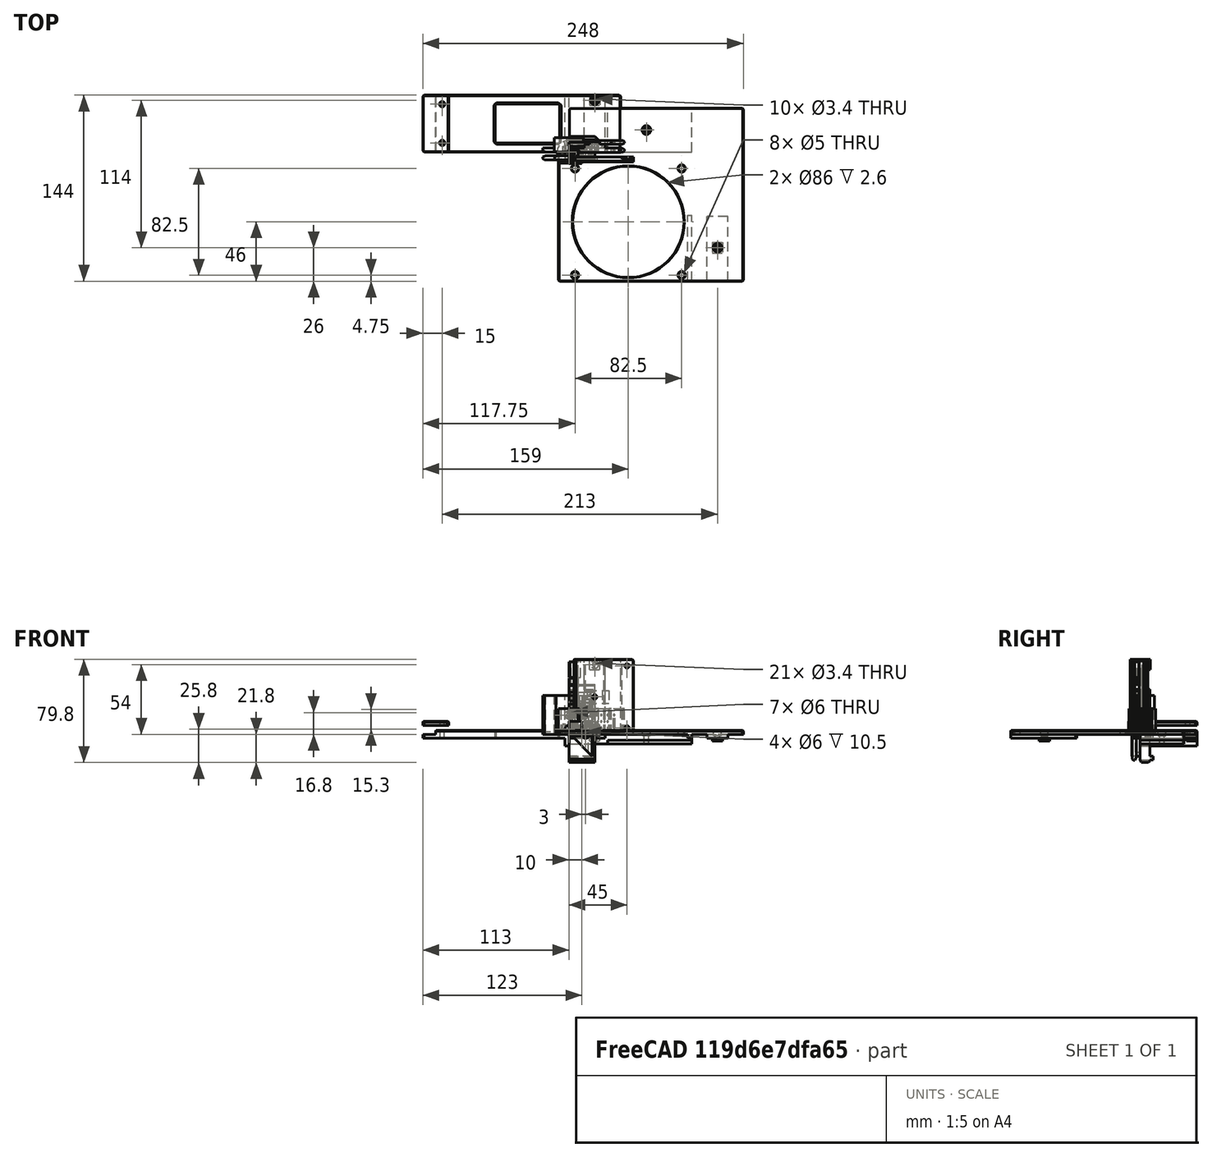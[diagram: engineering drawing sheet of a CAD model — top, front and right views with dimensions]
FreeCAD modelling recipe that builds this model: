
FCSTD DOCUMENT  (FreeCAD 0.18R16146 (Git))
Label: rack-clip-mounter
License: All rights reserved
LicenseURL: http://en.wikipedia.org/wiki/All_rights_reserved
objects: Part::Box×87, Part::Chamfer×70, Part::Cylinder×50, Part::MultiFuse×40, Part::Cut×40, Part::Feature×20, Part::MultiCommon×4, Part::Sphere×3, Part::FeaturePython×1
note: 315 computed .brp shape members not serialized (recipe doc carries the construction recipe); baked Part::Feature solids carry a one-line shape summary decoded from their .brp

FEATURE [Part::Box] Box  label="Cube"
  AttacherType = Attacher::AttachEngine3D
  Height = 8
  Length = 2.5
  Placement = pos=(-4.5,0,0) rot=(0,0,1;0rad)
  Width = 3.5
FEATURE [Part::Cylinder] Cylinder
  Angle = 360
  AttacherType = Attacher::AttachEngine3D
  Height = 8
  Placement = pos=(-4,2.5,0) rot=(0,0,1;0rad)
  Radius = 1
FEATURE [Part::Cylinder] Cylinder001
  Angle = 360
  AttacherType = Attacher::AttachEngine3D
  Height = 8
  Placement = pos=(4,2.5,0) rot=(0,0,1;0rad)
  Radius = 1
FEATURE [Part::Box] Box001  label="Cube001"
  AttacherType = Attacher::AttachEngine3D
  Height = 8
  Length = 2.5
  Placement = pos=(2,0,0) rot=(0,0,1;0rad)
  Width = 3.5
FEATURE [Part::Box] Box002  label="Cube002"
  AttacherType = Attacher::AttachEngine3D
  Height = 20
  Length = 16
  Placement = pos=(-8,-2.5,0) rot=(0,0,1;0rad)
  Width = 2.5
FEATURE [Part::Box] Box003  label="Cube003"
  AttacherType = Attacher::AttachEngine3D
  Height = 3
  Length = 10
  Width = 7
FEATURE [Part::Box] Box004  label="Cube004"
  AttacherType = Attacher::AttachEngine3D
  Height = 10
  Length = 10
  Placement = pos=(0,4,0) rot=(0,0,1;0rad)
  Width = 3
FEATURE [Part::Box] Box005  label="Cube005"
  AttacherType = Attacher::AttachEngine3D
  Height = 10
  Length = 10
  Placement = pos=(0,-9,0) rot=(0,0,1;0rad)
  Width = 9
FEATURE [Part::MultiFuse] Fusion001
  Shapes = -> [Box005,Box003,Box004]
FEATURE [Part::Box] Box006  label="Cube006"
  AttacherType = Attacher::AttachEngine3D
  Height = 20
  Length = 16
  Placement = pos=(-8,-8,0) rot=(0,0,1;0rad)
  Width = 2.5
FEATURE [Part::Box] Box007  label="Cube007"
  AttacherType = Attacher::AttachEngine3D
  Height = 20
  Length = 3
  Placement = pos=(5,-8,0) rot=(0,0,1;0rad)
  Width = 8
FEATURE [Part::MultiFuse] Fusion
  Shapes = -> [Cylinder,Box006,Box,Box007,Cylinder001,Box001,Box002]
FEATURE [Part::Chamfer] Chamfer
  Base = -> Fusion
  Edges = 1 edges: [Edge50 r1=2 r2=1]
FEATURE [Part::Chamfer] Chamfer001
  Base = -> Chamfer
  Edges = 1 edges: [Edge71 r1=2 r2=1]
FEATURE [Part::Chamfer] Chamfer002
  Base = -> Chamfer001
  Edges = 1 edges r=1: [Edge32]
FEATURE [Part::Box] Box008  label="Cube008"
  AttacherType = Attacher::AttachEngine3D
  Height = 8
  Length = 2.5
  Placement = pos=(-4.5,2.5,0) rot=(0,0,1;0rad)
  Width = 2
FEATURE [Part::Box] Box009  label="Cube009"
  AttacherType = Attacher::AttachEngine3D
  Height = 8
  Length = 2.5
  Placement = pos=(2,2.5,0) rot=(0,0,1;0rad)
  Width = 2
FEATURE [Part::MultiFuse] Fusion002
  Shapes = -> [Chamfer002,Box008,Box009]
FEATURE [Part::Cylinder] Cylinder002
  Angle = 360
  AttacherType = Attacher::AttachEngine3D
  Height = 10
  Placement = pos=(0,-5,4) rot=(1,0,0;1.5708rad)
  Radius = 3
FEATURE [Part::Cut] Cut  label="side-clip"
  Base = -> Fusion002
  Tool = -> Cylinder002
FEATURE [Part::Box] Box010  label="Cube010"
  AttacherType = Attacher::AttachEngine3D
  Height = 30
  Length = 22.6
  Placement = pos=(-11.3,0,0) rot=(0,0,1;0rad)
  Width = 11
FEATURE [Part::Box] Box011  label="Cube011"
  AttacherType = Attacher::AttachEngine3D
  Height = 30
  Length = 6
  Placement = pos=(-3,-6,0) rot=(0,0,1;0rad)
  Width = 6
FEATURE [Part::Box] Box012  label="Cube012"
  AttacherType = Attacher::AttachEngine3D
  Height = 30
  Length = 40
  Placement = pos=(-20,0,0) rot=(0,0,1;0rad)
  Width = 3
FEATURE [Part::Box] Box013  label="Cube013"
  AttacherType = Attacher::AttachEngine3D
  Height = 30
  Length = 40
  Placement = pos=(-20,-6,0) rot=(0,0,1;0rad)
  Width = 3
FEATURE [Part::Cylinder] Cylinder003
  Angle = 360
  AttacherType = Attacher::AttachEngine3D
  Height = 30
  Placement = pos=(0,5,15) rot=(1,0,0;1.5708rad)
  Radius = 3
FEATURE [Part::Cylinder] Cylinder004
  Angle = 360
  AttacherType = Attacher::AttachEngine3D
  Height = 30
  Placement = pos=(0,18,15) rot=(1,0,0;1.5708rad)
  Radius = 1.7
FEATURE [Part::Box] Box014  label="Cube014"
  AttacherType = Attacher::AttachEngine3D
  Height = 30
  Length = 22.6
  Placement = pos=(-11.3,0,0) rot=(0,0,1;0rad)
  Width = 11
FEATURE [Part::Box] Box015  label="Cube015"
  AttacherType = Attacher::AttachEngine3D
  Height = 30
  Length = 3.3
  Placement = pos=(8,-6,0) rot=(0,0,1;0rad)
  Width = 6
FEATURE [Part::Box] Box016  label="Cube016"
  AttacherType = Attacher::AttachEngine3D
  Height = 30
  Length = 20
  Placement = pos=(-11,-6,0) rot=(0,0,1;0rad)
  Width = 3
FEATURE [Part::Cylinder] Cylinder005
  Angle = 360
  AttacherType = Attacher::AttachEngine3D
  Height = 25
  Placement = pos=(0,5,15) rot=(1,0,0;1.5708rad)
  Radius = 3
FEATURE [Part::MultiFuse] Fusion004
  Shapes = -> [Box016,Box014,Box015]
FEATURE [Part::Chamfer] Chamfer008
  Base = -> Fusion004
  Edges = 1 edges r=1: [Edge24]
FEATURE [Part::Chamfer] Chamfer009
  Base = -> Chamfer008
  Edges = 1 edges: [Edge38 r1=1 r2=2]
FEATURE [Part::Chamfer] Chamfer010
  Base = -> Chamfer009
  Edges = 1 edges: [Edge39 r1=2 r2=1]
FEATURE [Part::Cylinder] Cylinder006
  Angle = 360
  AttacherType = Attacher::AttachEngine3D
  Height = 25
  Placement = pos=(0,16,15) rot=(1,0,0;1.5708rad)
  Radius = 1.7
FEATURE [Part::Cut] Cut003
  Base = -> Chamfer010
  Tool = -> Cylinder006
FEATURE [Part::Cut] Cut004
  Base = -> Cut003
  Tool = -> Cylinder005
FEATURE [Part::Chamfer] Chamfer011  label="clip-back-top-bottom"
  Base = -> Cut004
  Edges = 1 edges r=1: [Edge23]
FEATURE [Part::Cylinder] Cylinder007
  Angle = 360
  AttacherType = Attacher::AttachEngine3D
  Height = 2
  Radius = 1.7
FEATURE [Part::Cylinder] Cylinder008
  Angle = 360
  AttacherType = Attacher::AttachEngine3D
  Height = 2
  Radius = 9
FEATURE [Part::Cut] Cut005  label="washer"
  Base = -> Cylinder008
  Tool = -> Cylinder007
FEATURE [Part::MultiFuse] Fusion005
  Shapes = -> [Box010,Box012,Box011,Box013]
FEATURE [Part::Chamfer] Chamfer012
  Base = -> Fusion005
  Edges = 3 edges: [Edge29 r1=2 r2=1,Edge55 r1=2 r2=1,Edge59 r1=2 r2=1]
FEATURE [Part::Chamfer] Chamfer013
  Base = -> Chamfer012
  Edges = 1 edges: [Edge48 r1=1 r2=2]
FEATURE [Part::Chamfer] Chamfer014
  Base = -> Chamfer013
  Edges = 2 edges r=1: [Edge85,Edge86]
FEATURE [Part::Cut] Cut006
  Base = -> Chamfer014
  Tool = -> Cylinder003
FEATURE [Part::Cut] Cut007  label="ckip-back-mid"
  Base = -> Cut006
  Tool = -> Cylinder004
FEATURE [Part::Box] Box017  label="Cube017"
  AttacherType = Attacher::AttachEngine3D
  Height = 41.6
  Length = 20
  Placement = pos=(0,0,-3) rot=(0,0,1;0rad)
  Width = 4.5
FEATURE [Part::Box] Box018  label="Cube018"
  AttacherType = Attacher::AttachEngine3D
  Height = 8.5
  Length = 20
  Placement = pos=(0,-6,-3) rot=(0,0,1;0rad)
  Width = 6
FEATURE [Part::Box] Box019  label="Cube019"
  AttacherType = Attacher::AttachEngine3D
  Height = 30
  Length = 20
  Placement = pos=(0,-6,-3) rot=(0,0,1;0rad)
  Width = 3
FEATURE [Part::Cylinder] Cylinder009
  Angle = 360
  AttacherType = Attacher::AttachEngine3D
  Height = 17
  Placement = pos=(10,3,19.3) rot=(1,0,0;1.5708rad)
  Radius = 3
FEATURE [Part::Cylinder] Cylinder010
  Angle = 360
  AttacherType = Attacher::AttachEngine3D
  Height = 17
  Placement = pos=(10,6,19.3) rot=(1,0,0;1.5708rad)
  Radius = 1.7
FEATURE [Part::Cylinder] Cylinder011
  Angle = 360
  AttacherType = Attacher::AttachEngine3D
  Height = 2
  Placement = pos=(10,5.5,19.3) rot=(1,0,0;1.5708rad)
  Radius = 2.9
FEATURE [Part::Box] Box020  label="Cube020"
  AttacherType = Attacher::AttachEngine3D
  Height = 3
  Length = 20
  Placement = pos=(0,-6,-3) rot=(0,0,1;0rad)
  Width = 13
FEATURE [Part::Box] Box021  label="Cube021"
  AttacherType = Attacher::AttachEngine3D
  Height = 41.6
  Length = 20
  Placement = pos=(0,0,-3) rot=(0,0,1;0rad)
  Width = 4.5
FEATURE [Part::Box] Box022  label="Cube022"
  AttacherType = Attacher::AttachEngine3D
  Height = 3
  Length = 20
  Placement = pos=(0,0,-3) rot=(0,0,1;0rad)
  Width = 7
FEATURE [Part::Box] Box023  label="Cube023"
  AttacherType = Attacher::AttachEngine3D
  Height = 8.5
  Length = 20
  Placement = pos=(0,-6,30.1) rot=(0,0,1;0rad)
  Width = 6
FEATURE [Part::Box] Box024  label="Cube024"
  AttacherType = Attacher::AttachEngine3D
  Height = 30
  Length = 20
  Placement = pos=(0,-6,8.6) rot=(0,0,1;0rad)
  Width = 3
FEATURE [Part::MultiFuse] Fusion007
  Shapes = -> [Box024,Box023,Box022,Box021]
FEATURE [Part::Cylinder] Cylinder012
  Angle = 360
  AttacherType = Attacher::AttachEngine3D
  Height = 15
  Placement = pos=(10,7,19.3) rot=(1,0,0;1.5708rad)
  Radius = 1.7
FEATURE [Part::Chamfer] Chamfer015
  Base = -> Cylinder011
  Edges = 1 edges r=1: [Edge3]
FEATURE [Part::MultiFuse] Fusion008
  Shapes = -> [Box019,Box018,Box017,Box020]
FEATURE [Part::Chamfer] Chamfer016
  Base = -> Fusion008
  Edges = 1 edges: [Edge36 r1=1 r2=2]
FEATURE [Part::Chamfer] Chamfer017
  Base = -> Chamfer016
  Edges = 1 edges r=1: [Edge34]
FEATURE [Part::MultiFuse] Fusion009
  Shapes = -> [Chamfer017,Chamfer015]
FEATURE [Part::Cut] Cut008
  Base = -> Fusion009
  Tool = -> Cylinder010
FEATURE [Part::Chamfer] Chamfer018
  Base = -> Cut008
  Edges = 1 edges r=1: [Edge77]
FEATURE [Part::Cut] Cut009  label="clip-side-bottom-corner"
  Base = -> Chamfer018
  Tool = -> Cylinder009
FEATURE [Part::Cylinder] Cylinder013
  Angle = 360
  AttacherType = Attacher::AttachEngine3D
  Height = 2
  Placement = pos=(10,5.5,19.3) rot=(1,0,0;1.5708rad)
  Radius = 2.9
FEATURE [Part::Cylinder] Cylinder014
  Angle = 360
  AttacherType = Attacher::AttachEngine3D
  Height = 15
  Placement = pos=(10,3,19.3) rot=(1,0,0;1.5708rad)
  Radius = 3
FEATURE [Part::Chamfer] Chamfer019
  Base = -> Cylinder013
  Edges = 1 edges r=1: [Edge3]
FEATURE [Part::Chamfer] Chamfer020
  Base = -> Fusion007
  Edges = 1 edges: [Edge13 r1=2 r2=1]
FEATURE [Part::Chamfer] Chamfer021
  Base = -> Chamfer020
  Edges = 3 edges r=1: [Edge14,Edge23,Edge38]
FEATURE [Part::MultiFuse] Fusion010
  Shapes = -> [Chamfer021,Chamfer019]
FEATURE [Part::Cut] Cut010
  Base = -> Fusion010
  Tool = -> Cylinder012
FEATURE [Part::Cut] Cut011  label="clip-side-top-corner"
  Base = -> Cut010
  Tool = -> Cylinder014
FEATURE [Part::Box] Box025  label="Cube025"
  AttacherType = Attacher::AttachEngine3D
  Height = 36.6
  Length = 20
  Placement = pos=(0,0,-3) rot=(0,0,1;0rad)
  Width = 7.5
FEATURE [Part::Box] Box026  label="Cube026"
  AttacherType = Attacher::AttachEngine3D
  Height = 6
  Length = 20
  Placement = pos=(0,-6,-3) rot=(0,0,1;0rad)
  Width = 6
FEATURE [Part::Box] Box027  label="Cube027"
  AttacherType = Attacher::AttachEngine3D
  Height = 3
  Length = 20
  Placement = pos=(0,-6,-3) rot=(0,0,1;0rad)
  Width = 16
FEATURE [Part::Box] Box028  label="Cube028"
  AttacherType = Attacher::AttachEngine3D
  Height = 27.5
  Length = 20
  Placement = pos=(0,-6,-3) rot=(0,0,1;0rad)
  Width = 3
FEATURE [Part::Cylinder] Cylinder015
  Angle = 360
  AttacherType = Attacher::AttachEngine3D
  Height = 20
  Placement = pos=(10,5,16.8) rot=(1,0,0;1.5708rad)
  Radius = 3
FEATURE [Part::Cylinder] Cylinder016
  Angle = 360
  AttacherType = Attacher::AttachEngine3D
  Height = 20
  Placement = pos=(10,12,16.8) rot=(1,0,0;1.5708rad)
  Radius = 1.7
FEATURE [Part::Cylinder] Cylinder017
  Angle = 360
  AttacherType = Attacher::AttachEngine3D
  Height = 20
  Placement = pos=(10,12,16.8) rot=(1,0,0;1.5708rad)
  Radius = 1.7
FEATURE [Part::Cylinder] Cylinder018
  Angle = 360
  AttacherType = Attacher::AttachEngine3D
  Height = 20
  Placement = pos=(10,5,16.8) rot=(1,0,0;1.5708rad)
  Radius = 3
FEATURE [Part::Box] Box029  label="Cube029"
  AttacherType = Attacher::AttachEngine3D
  Height = 27.5
  Length = 20
  Placement = pos=(0,-6,6.1) rot=(0,0,1;0rad)
  Width = 3
FEATURE [Part::Box] Box030  label="Cube030"
  AttacherType = Attacher::AttachEngine3D
  Height = 3
  Length = 20
  Placement = pos=(0,0,-3) rot=(0,0,1;0rad)
  Width = 10
FEATURE [Part::Box] Box031  label="Cube031"
  AttacherType = Attacher::AttachEngine3D
  Height = 6
  Length = 20
  Placement = pos=(0,-6,27.6) rot=(0,0,1;0rad)
  Width = 6
FEATURE [Part::Box] Box032  label="Cube032"
  AttacherType = Attacher::AttachEngine3D
  Height = 36.6
  Length = 20
  Placement = pos=(0,0,-3) rot=(0,0,1;0rad)
  Width = 7.5
FEATURE [Part::MultiFuse] Fusion011
  Shapes = -> [Box028,Box026,Box025,Box027]
FEATURE [Part::Chamfer] Chamfer022
  Base = -> Fusion011
  Edges = 1 edges: [Edge36 r1=1 r2=2]
FEATURE [Part::Chamfer] Chamfer023
  Base = -> Chamfer022
  Edges = 3 edges r=1: [Edge7,Edge31,Edge34]
FEATURE [Part::Cut] Cut012
  Base = -> Chamfer023
  Tool = -> Cylinder015
FEATURE [Part::Cut] Cut013  label="clip-side-bottom-center"
  Base = -> Cut012
  Tool = -> Cylinder016
FEATURE [Part::MultiFuse] Fusion012
  Shapes = -> [Box029,Box031,Box032,Box030]
FEATURE [Part::Chamfer] Chamfer024
  Base = -> Fusion012
  Edges = 1 edges: [Edge13 r1=2 r2=1]
FEATURE [Part::Chamfer] Chamfer025
  Base = -> Chamfer024
  Edges = 3 edges r=1: [Edge14,Edge23,Edge38]
FEATURE [Part::Cut] Cut014
  Base = -> Chamfer025
  Tool = -> Cylinder018
FEATURE [Part::Cut] Cut015  label="clip-side-top-center"
  Base = -> Cut014
  Tool = -> Cylinder017
FEATURE [Part::Box] Box033  label="Cube033"
  AttacherType = Attacher::AttachEngine3D
  Height = 43.6
  Length = 20
  Placement = pos=(0,0,-21.8) rot=(0,0,1;0rad)
  Width = 7.5
FEATURE [Part::Box] Box034  label="Cube034"
  AttacherType = Attacher::AttachEngine3D
  Height = 3
  Length = 20
  Placement = pos=(0,0,-19.8) rot=(0,0,1;0rad)
  Width = 10
FEATURE [Part::Box] Box035  label="Cube035"
  AttacherType = Attacher::AttachEngine3D
  Height = 6
  Length = 20
  Placement = pos=(0,-6,-3) rot=(0,0,1;0rad)
  Width = 6
FEATURE [Part::Box] Box036  label="Cube036"
  AttacherType = Attacher::AttachEngine3D
  Height = 40
  Length = 20
  Placement = pos=(0,-6,-20) rot=(0,0,1;0rad)
  Width = 3
FEATURE [Part::MultiFuse] Fusion013
  Shapes = -> [Box036,Box035,Box034,Box033]
FEATURE [Part::Chamfer] Chamfer026
  Base = -> Fusion013
  Edges = 1 edges: [Edge30 r1=1 r2=2]
FEATURE [Part::Chamfer] Chamfer027
  Base = -> Chamfer026
  Edges = 1 edges: [Edge45 r1=2 r2=1]
FEATURE [Part::Chamfer] Chamfer028
  Base = -> Chamfer027
  Edges = 1 edges: [Edge57 r1=2 r2=1]
FEATURE [Part::Chamfer] Chamfer029
  Base = -> Chamfer028
  Edges = 1 edges: [Edge64 r1=1.9 r2=1]
FEATURE [Part::Chamfer] Chamfer030
  Base = -> Chamfer029
  Edges = 4 edges r=1: [Edge14,Edge44,Edge85,Edge86]
FEATURE [Part::Cylinder] Cylinder019
  Angle = 360
  AttacherType = Attacher::AttachEngine3D
  Height = 19
  Placement = pos=(10,4.5,-1e-15) rot=(1,0,0;1.5708rad)
  Radius = 3
FEATURE [Part::Cylinder] Cylinder020
  Angle = 360
  AttacherType = Attacher::AttachEngine3D
  Height = 19
  Placement = pos=(10,9,-2e-15) rot=(1,0,0;1.5708rad)
  Radius = 1.7
FEATURE [Part::Cut] Cut016
  Base = -> Chamfer030
  Tool = -> Cylinder020
FEATURE [Part::Cut] Cut017  label="clip-side-mid-center"
  Base = -> Cut016
  Tool = -> Cylinder019
FEATURE [Part::Box] Box037  label="Cube037"
  AttacherType = Attacher::AttachEngine3D
  Height = 36.6
  Length = 18
  Placement = pos=(0,0,-19.8) rot=(0,0,1;0rad)
  Width = 7.5
FEATURE [Part::Box] Box038  label="Cube038"
  AttacherType = Attacher::AttachEngine3D
  Height = 3
  Length = 18
  Placement = pos=(0,0,-19.8) rot=(0,0,1;0rad)
  Width = 10
FEATURE [Part::Box] Box039  label="Cube039"
  AttacherType = Attacher::AttachEngine3D
  Height = 3.6
  Length = 18
  Placement = pos=(0,-6.5,-1.8) rot=(0,0,1;0rad)
  Width = 8
FEATURE [Part::Feature] Body001
  shape: bbox 18 x 6.5 x 18 mm, 5 faces (baked)
FEATURE [Part::Feature] Body002
  Placement = pos=(-3,3,3) rot=(0,0,1;0rad)
  shape: bbox 18 x 6.5 x 18 mm, 5 faces (baked)
FEATURE [Part::Cut] Cut018  label="corner-mount-slot"
  Base = -> Body001
  Placement = pos=(0,0,-1.2) rot=(0,0,1;0rad)
  Tool = -> Body002
FEATURE [Part::Feature] Cut018001  label="Cut019"
  Placement = pos=(0,0,-1.2) rot=(0,0,1;0rad)
  shape: bbox 18 x 6.5 x 18 mm, 8 faces (baked)
FEATURE [Part::Feature] Part__Mirroring001  label="Cut019 (Mirror #1)001"
  Placement = pos=(0,0,1e-16) rot=(0,0,1;0rad)
  shape: bbox 18 x 6.5 x 18 mm, 8 faces (baked)
FEATURE [Part::Cylinder] Cylinder021
  Angle = 360
  AttacherType = Attacher::AttachEngine3D
  Height = 23
  Placement = pos=(13,12,-3e-15) rot=(1,0,0;1.5708rad)
  Radius = 1.7
FEATURE [Part::MultiFuse] Fusion014
  Shapes = -> [Cut018001,Part__Mirroring001,Box039,Box038,Box037]
FEATURE [Part::Cylinder] Cylinder022
  Angle = 360
  AttacherType = Attacher::AttachEngine3D
  Height = 23
  Placement = pos=(13,4,-1.2e-15) rot=(1,0,0;1.5708rad)
  Radius = 3
FEATURE [Part::Cut] Cut018002
  Base = -> Fusion014
  Tool = -> Cylinder021
FEATURE [Part::Cut] Cut018003  label="acrilic-mid-cirner"
  Base = -> Cut018002
  Tool = -> Cylinder022
FEATURE [Part::Feature] Cut018004  label="side-clip001"
  shape: bbox 16 x 12.5 x 20 mm, 71 faces (baked)
FEATURE [Part::Box] Box040  label="Cube040"
  AttacherType = Attacher::AttachEngine3D
  Height = 24
  Length = 22
  Placement = pos=(-12,-5,0) rot=(0,0,1;0rad)
  Width = 14
FEATURE [Part::Feature] Cut018005  label="side-clip002"
  shape: bbox 16 x 12.5 x 20 mm, 71 faces (baked)
FEATURE [Part::Box] Box041  label="Cube041"
  AttacherType = Attacher::AttachEngine3D
  Height = 24
  Length = 22
  Placement = pos=(-12,-17,0) rot=(0,0,1;0rad)
  Width = 14
FEATURE [Part::MultiCommon] Common
  Placement = pos=(0,-0.5,0) rot=(0,0,1;0rad)
  Shapes = -> [Box041,Cut018004]
FEATURE [Part::MultiCommon] Common001
  Shapes = -> [Cut018005,Box040]
FEATURE [Part::MultiFuse] Fusion015  label="side-clip-wide"
  Shapes = -> [Common,Common001]
FEATURE [Part::Feature] Cut018006  label="corner-mount-slot001"
  Placement = pos=(2,0,17) rot=(0,0,1;0rad)
  shape: bbox 18 x 6.5 x 18 mm, 8 faces (baked)
FEATURE [Part::Box] Box042  label="Cube042"
  AttacherType = Attacher::AttachEngine3D
  Height = 38
  Length = 20
  Placement = pos=(0,0,-3) rot=(0,0,1;0rad)
  Width = 7.5
FEATURE [Part::Box] Box043  label="Cube043"
  AttacherType = Attacher::AttachEngine3D
  Height = 3
  Length = 20
  Placement = pos=(0,0,-3) rot=(0,0,1;0rad)
  Width = 10
FEATURE [Part::Cylinder] Cylinder023
  Angle = 360
  AttacherType = Attacher::AttachEngine3D
  Height = 21
  Placement = pos=(10,4,16.8) rot=(1,0,0;1.5708rad)
  Radius = 3
FEATURE [Part::MultiFuse] Fusion016
  Shapes = -> [Box043,Cut018006,Box042]
FEATURE [Part::Cylinder] Cylinder024
  Angle = 360
  AttacherType = Attacher::AttachEngine3D
  Height = 21
  Placement = pos=(10,12,16.8) rot=(1,0,0;1.5708rad)
  Radius = 1.7
FEATURE [Part::Cut] Cut018007
  Base = -> Fusion016
  Tool = -> Cylinder024
FEATURE [Part::Cut] Cut018008
  Base = -> Cut018007
  Tool = -> Cylinder023
FEATURE [Part::Chamfer] Chamfer031  label="acrilic-corner-btm"
  Base = -> Cut018008
  Edges = 1 edges r=1: [Edge5]
FEATURE [Part::Box] Box044  label="Cube044"
  AttacherType = Attacher::AttachEngine3D
  Height = 36.6
  Length = 20
  Placement = pos=(0,0,-3) rot=(0,0,1;0rad)
  Width = 7.5
FEATURE [Part::Feature] Part__Mirroring002  label="corner-mount-slot002 (Mirror #1)001"
  Placement = pos=(2,0,15.4) rot=(0,0,1;0rad)
  shape: bbox 18 x 6.5 x 18 mm, 8 faces (baked)
FEATURE [Part::Box] Box045  label="Cube045"
  AttacherType = Attacher::AttachEngine3D
  Height = 3
  Length = 20
  Placement = pos=(0,0,-3) rot=(0,0,1;0rad)
  Width = 10
FEATURE [Part::MultiFuse] Fusion017
  Shapes = -> [Box045,Part__Mirroring002,Box044]
FEATURE [Part::Chamfer] Chamfer032
  Base = -> Fusion017
  Edges = 2 edges r=1: [Edge5,Edge32]
FEATURE [Part::Cylinder] Cylinder025
  Angle = 360
  AttacherType = Attacher::AttachEngine3D
  Height = 21
  Placement = pos=(10,12,16.8) rot=(1,0,0;1.5708rad)
  Radius = 1.7
FEATURE [Part::Cylinder] Cylinder026
  Angle = 360
  AttacherType = Attacher::AttachEngine3D
  Height = 21
  Placement = pos=(10,4,16.8) rot=(1,0,0;1.5708rad)
  Radius = 3
FEATURE [Part::Cut] Cut018009
  Base = -> Chamfer032
  Tool = -> Cylinder025
FEATURE [Part::Cut] Cut018010  label="acrilic-corner-top"
  Base = -> Cut018009
  Tool = -> Cylinder026
FEATURE [Part::Box] Box051008  label="Cube065"
  AttacherType = Attacher::AttachEngine3D
  Height = 3
  Length = 9
  Placement = pos=(-8,-100,0) rot=(0,0,1;0rad)
  Width = 99
FEATURE [Part::Chamfer] Chamfer034004
  Base = -> Box051008
  Edges = 2 edges r=1: [Edge1,Edge3]
FEATURE [Part::Chamfer] Chamfer034005
  Base = -> Chamfer034004
  Edges = 5 edges r=0.4: [Edge1,Edge5,Edge6,Edge7,Edge8]
FEATURE [Part::Feature] Chamfer034005001  label="Chamfer034006"
  shape: bbox 9 x 99 x 3 mm, 13 faces (baked)
FEATURE [Part::Box] Box051009  label="Cube066"
  AttacherType = Attacher::AttachEngine3D
  Height = 3
  Length = 40
  Width = 44
FEATURE [Part::Box] Box051010  label="Cube067"
  AttacherType = Attacher::AttachEngine3D
  Height = 3
  Length = 16
  Placement = pos=(12,0,-3) rot=(0,0,1;0rad)
  Width = 44
FEATURE [Part::Box] Box051011  label="Cube068"
  AttacherType = Attacher::AttachEngine3D
  Height = 3
  Length = 8
  Placement = pos=(16,36,-5) rot=(0,0,1;0rad)
  Width = 8
FEATURE [Part::Feature] Chamfer034005002001  label="Chamfer034005003"
  shape: bbox 135 x 134 x 10.5 mm, 37 faces (baked)
FEATURE [Part::Chamfer] Chamfer034005002002
  Base = -> Chamfer034005002001
  Edges = 15 edges r=0.4: [Edge1,Edge18,Edge42,Edge43,Edge46,Edge70,Edge78,Edge79,Edge81,Edge83,Edge85,Edge87,Edge89,Edge93,Edge95]
FEATURE [Part::MultiFuse] Fusion021005002  label="fan-mount-btm"
  Shapes = -> [Chamfer034005,Chamfer034005002002]
FEATURE [Part::Feature] Cut018011002001  label="Cut018011003"
  shape: bbox 135 x 134 x 10.5 mm, 35 faces (baked)
FEATURE [Part::Chamfer] Chamfer034005002003
  Base = -> Cut018011002001
  Edges = 4 edges r=1: [Edge41,Edge43,Edge80,Edge82]
FEATURE [Part::Chamfer] Chamfer034005002004
  Base = -> Chamfer034005002003
  Edges = 15 edges r=0.4: [Edge25,Edge33,Edge36,Edge50,Edge58,Edge61,Edge64,Edge65,Edge67,Edge69,Edge71,Edge73,Edge75,Edge76,Edge77]
FEATURE [Part::MultiFuse] Fusion021005003  label="fan-mount-top"
  Shapes = -> [Chamfer034005001,Chamfer034005002004]
FEATURE [Part::MultiFuse] Fusion021005004
  Shapes = -> [Box051011,Box051010,Box051009]
FEATURE [Part::Box] Box051012  label="Cube069"
  AttacherType = Attacher::AttachEngine3D
  Height = 6
  Length = 103
  Placement = pos=(-103,0,-3) rot=(0,0,1;0rad)
  Width = 44
FEATURE [Part::Box] Box051013  label="Cube070"
  AttacherType = Attacher::AttachEngine3D
  Height = 3
  Length = 10
  Placement = pos=(-113,0,-3) rot=(0,0,1;0rad)
  Width = 44
FEATURE [Part::Box] Box051014  label="Cube071"
  AttacherType = Attacher::AttachEngine3D
  Height = 6
  Length = 50
  Placement = pos=(-57,7,-3) rot=(0,0,1;0rad)
  Width = 30
FEATURE [Part::Box] Box051015  label="Cube072"
  AttacherType = Attacher::AttachEngine3D
  Height = 6
  Length = 3
  Placement = pos=(-3,0,-9) rot=(0,0,1;0rad)
  Width = 44
FEATURE [Part::Cylinder] Cylinder027
  Angle = 360
  AttacherType = Attacher::AttachEngine3D
  Height = 10
  Placement = pos=(20,40,-5) rot=(0,0,1;0rad)
  Radius = 1.7
FEATURE [Part::Cylinder] Cylinder028
  Angle = 360
  AttacherType = Attacher::AttachEngine3D
  Height = 10
  Placement = pos=(20,40,-1) rot=(0,0,1;0rad)
  Radius = 3
FEATURE [Part::MultiFuse] Fusion021005005
  Shapes = -> [Cylinder028,Cylinder027]
FEATURE [Part::MultiFuse] Fusion021005006
  Shapes = -> [Box051012,Box051013,Box051015,Fusion021005004]
FEATURE [Part::Cut] Cut018011002002
  Base = -> Fusion021005006
  Tool = -> Fusion021005005
FEATURE [Part::Cut] Cut018011002003
  Base = -> Cut018011002002
  Tool = -> Box051014
FEATURE [Part::Box] Box051016  label="Cube073"
  AttacherType = Attacher::AttachEngine3D
  Height = 3
  Length = 20
  Placement = pos=(-113,0,7) rot=(0,0,1;0rad)
  Width = 44
FEATURE [Part::Cylinder] Cylinder029
  Angle = 360
  AttacherType = Attacher::AttachEngine3D
  Height = 30
  Placement = pos=(-98,7,-7) rot=(0,0,1;0rad)
  Radius = 1.7
FEATURE [Part::Cylinder] Cylinder030
  Angle = 360
  AttacherType = Attacher::AttachEngine3D
  Height = 30
  Placement = pos=(-98,37,-7) rot=(0,0,1;0rad)
  Radius = 1.7
FEATURE [Part::Cylinder] Cylinder031
  Angle = 360
  AttacherType = Attacher::AttachEngine3D
  Height = 30
  Placement = pos=(-98,37,-7) rot=(0,0,1;0rad)
  Radius = 1.7
FEATURE [Part::Cylinder] Cylinder032
  Angle = 360
  AttacherType = Attacher::AttachEngine3D
  Height = 30
  Placement = pos=(-98,7,-7) rot=(0,0,1;0rad)
  Radius = 1.7
FEATURE [Part::MultiFuse] Fusion021005007
  Shapes = -> [Cylinder032,Cylinder031]
FEATURE [Part::Cut] Cut018011002004
  Base = -> Cut018011002003
  Tool = -> Fusion021005007
FEATURE [Part::MultiFuse] Fusion021005008
  Shapes = -> [Cylinder029,Cylinder030]
FEATURE [Part::Cut] Cut018011002005
  Base = -> Box051016
  Tool = -> Fusion021005008
FEATURE [Part::Chamfer] Chamfer034005002005
  Base = -> Cut018011002004
  Edges = 12 edges r=1: [Edge15,Edge16,Edge17,Edge18,Edge43,Edge46,Edge52,Edge53,Edge54,Edge55,Edge62,Edge64]
FEATURE [Part::Chamfer] Chamfer034005002006  label="cable-route-base"
  Base = -> Chamfer034005002005
  Edges = 11 edges r=0.4: [Edge9,Edge10,Edge11,Edge13,Edge14,Edge44,Edge45,Edge46,Edge47,Edge48,Edge49]
FEATURE [Part::Chamfer] Chamfer034005002007
  Base = -> Cut018011002005
  Edges = 4 edges r=1: [Edge1,Edge3,Edge6,Edge13]
FEATURE [Part::Chamfer] Chamfer034005002008  label="cable-route-cap"
  Base = -> Chamfer034005002007
  Edges = 10 edges r=0.4: [Edge1,Edge5,Edge6,Edge7,Edge8,Edge9,Edge10,Edge11,Edge12,Edge13]
FEATURE [Part::Box] Box051017  label="Cube074"
  AttacherType = Attacher::AttachEngine3D
  Height = 20
  Length = 33
  Width = 3
FEATURE [Part::Box] Box051018  label="Cube075"
  AttacherType = Attacher::AttachEngine3D
  Height = 20
  Length = 10
  Placement = pos=(0,6.5,0) rot=(0,0,1;0rad)
  Width = 3
FEATURE [Part::Box] Box051019  label="Cube076"
  AttacherType = Attacher::AttachEngine3D
  Height = 20
  Length = 20
  Placement = pos=(13,6,0) rot=(0,0,1;0rad)
  Width = 3
FEATURE [Part::Box] Box051020  label="Cube077"
  AttacherType = Attacher::AttachEngine3D
  Height = 20
  Length = 3
  Placement = pos=(10,3,0) rot=(0,0,1;0rad)
  Width = 6.5
FEATURE [Part::Chamfer] Chamfer034005002009
  Base = -> Box051020
  Edges = 1 edges r=0.5: [Edge7]
FEATURE [Part::Chamfer] Chamfer034005002010
  Base = -> Box051019
  Edges = 1 edges: [Edge5 r1=1 r2=2]
FEATURE [Part::Chamfer] Chamfer034005002011
  Base = -> Box051017
  Edges = 1 edges: [Edge7 r1=1 r2=2]
FEATURE [Part::Chamfer] Chamfer034005002012
  Base = -> Chamfer034005002011
  Edges = 1 edges: [Edge15 r1=2 r2=1]
FEATURE [Part::Chamfer] Chamfer034005002013
  Base = -> Box051018
  Edges = 1 edges: [Edge1 r1=1 r2=2]
FEATURE [Part::Sphere] Sphere
  Angle1 = -90
  Angle2 = 90
  Angle3 = 360
  AttacherType = Attacher::AttachEngine3D
  Placement = pos=(30,3,5) rot=(0,0,1;0rad)
  Radius = 0.5
FEATURE [Part::Sphere] Sphere001
  Angle1 = -90
  Angle2 = 90
  Angle3 = 360
  AttacherType = Attacher::AttachEngine3D
  Placement = pos=(30,3,15) rot=(0,0,1;0rad)
  Radius = 0.5
FEATURE [Part::Sphere] Sphere002
  Angle1 = -90
  Angle2 = 90
  Angle3 = 360
  AttacherType = Attacher::AttachEngine3D
  Placement = pos=(30,3,10) rot=(0,0,1;0rad)
  Radius = 0.5
FEATURE [Part::MultiFuse] Fusion021005009
  Shapes = -> [Sphere002,Sphere001,Sphere]
FEATURE [Part::Feature] Fusion021005009001  label="Fusion021005010"
  Placement = pos=(-5,0,0) rot=(0,0,1;0rad)
  shape: bbox 1 x 1 x 11 mm, 3 faces, 3 solids (baked)
FEATURE [Part::Feature] Fusion021005009002  label="Fusion021005011"
  Placement = pos=(-10,0,0) rot=(0,0,1;0rad)
  shape: bbox 1 x 1 x 11 mm, 3 faces, 3 solids (baked)
FEATURE [Part::Feature] Fusion021005009003  label="Fusion021005012"
  Placement = pos=(-12.5,3,0) rot=(0,0,1;0rad)
  shape: bbox 1 x 1 x 11 mm, 3 faces, 3 solids (baked)
FEATURE [Part::Feature] Fusion021005009004  label="Fusion021005013"
  Placement = pos=(-7.5,3,0) rot=(0,0,1;0rad)
  shape: bbox 1 x 1 x 11 mm, 3 faces, 3 solids (baked)
FEATURE [Part::Feature] Fusion021005009005  label="Fusion021005014"
  Placement = pos=(-2.5,3,0) rot=(0,0,1;0rad)
  shape: bbox 1 x 1 x 11 mm, 3 faces, 3 solids (baked)
FEATURE [Part::Chamfer] Chamfer034005002014
  Base = -> Chamfer034005002012
  Edges = 2 edges r=1: [Edge14,Edge16]
FEATURE [Part::Chamfer] Chamfer034005002015
  Base = -> Chamfer034005002013
  Edges = 1 edges r=1: [Edge3]
FEATURE [Part::Chamfer] Chamfer034005002016
  Base = -> Chamfer034005002010
  Edges = 1 edges r=1: [Edge3]
FEATURE [Part::MultiFuse] Fusion021005009006
  Shapes = -> [Chamfer034005002016,Chamfer034005002015,Chamfer034005002014,Fusion021005009005,Fusion021005009004,Fusion021005009003,Fusion021005009002,Fusion021005009001,Fusion021005009,Chamfer034005002009]
FEATURE [Part::Cylinder] Cylinder033
  Angle = 360
  AttacherType = Attacher::AttachEngine3D
  Height = 10
  Placement = pos=(22,1e-15,2.5) rot=(-1,0,0;1.5708rad)
  Radius = 0.6
FEATURE [Part::Cylinder] Cylinder034
  Angle = 360
  AttacherType = Attacher::AttachEngine3D
  Height = 10
  Placement = pos=(22,-1.8e-15,17.5) rot=(-1,0,0;1.5708rad)
  Radius = 0.6
FEATURE [Part::MultiFuse] Fusion021005009007
  Shapes = -> [Cylinder034,Cylinder033]
FEATURE [Part::Box] Box051021  label="Cube078"
  AttacherType = Attacher::AttachEngine3D
  Height = 15
  Length = 1.2
  Placement = pos=(21.4,0,2.5) rot=(0,0,1;0rad)
  Width = 1
FEATURE [Part::Box] Box051022  label="Cube079"
  AttacherType = Attacher::AttachEngine3D
  Height = 15
  Length = 1.2
  Placement = pos=(21.4,8,2.5) rot=(0,0,1;0rad)
  Width = 1
FEATURE [Part::MultiFuse] Fusion021005009008
  Shapes = -> [Box051022,Box051021,Fusion021005009007]
FEATURE [Part::Cut] Cut018011002006  label="acrylic-sheet-clip"
  Base = -> Fusion021005009006
  Tool = -> Fusion021005009008
FEATURE [Part::Box] Box051023  label="Cube080"
  AttacherType = Attacher::AttachEngine3D
  Height = 20
  Length = 43
  Width = 3
FEATURE [Part::Box] Box051024  label="Cube081"
  AttacherType = Attacher::AttachEngine3D
  Height = 20
  Length = 20
  Placement = pos=(0,9.5,0) rot=(0,0,1;0rad)
  Width = 2.5
FEATURE [Part::Box] Box051025  label="Cube082"
  AttacherType = Attacher::AttachEngine3D
  Height = 20
  Length = 20
  Placement = pos=(23,6,0) rot=(0,0,1;0rad)
  Width = 3
FEATURE [Part::Box] Box051026  label="Cube083"
  AttacherType = Attacher::AttachEngine3D
  Height = 20
  Length = 3
  Placement = pos=(20,3,0) rot=(0,0,1;0rad)
  Width = 9
FEATURE [Part::Chamfer] Chamfer034005002017
  Base = -> Box051026
  Edges = 1 edges r=2.9: [Edge7]
FEATURE [Part::Box] Box051027  label="Cube084"
  AttacherType = Attacher::AttachEngine3D
  Height = 20
  Length = 5
  Placement = pos=(0,8.75,0) rot=(0,0,1;0rad)
  Width = 3.25
FEATURE [Part::Chamfer] Chamfer034005002018
  Base = -> Box051027
  Edges = 1 edges r=1: [Edge1]
FEATURE [Part::Chamfer] Chamfer034005002019
  Base = -> Box051024
  Edges = 1 edges r=1: [Edge1]
FEATURE [Part::Chamfer] Chamfer034005002020
  Base = -> Box051023
  Edges = 2 edges r=1: [Edge1,Edge3]
FEATURE [Part::Chamfer] Chamfer034005002021
  Base = -> Chamfer034005002018
  Edges = 1 edges r=1: [Edge3]
FEATURE [Part::Chamfer] Chamfer034005002022
  Base = -> Chamfer034005002019
  Edges = 1 edges r=1: [Edge3]
FEATURE [Part::Chamfer] Chamfer034005002023
  Base = -> Chamfer034005002021
  Edges = 1 edges r=1: [Edge18]
FEATURE [Part::Chamfer] Chamfer034005002024
  Base = -> Chamfer034005002020
  Edges = 1 edges r=1: [Edge17]
FEATURE [Part::Chamfer] Chamfer034005002025
  Base = -> Box051025
  Edges = 1 edges r=1: [Edge7]
FEATURE [Part::Chamfer] Chamfer034005002026
  Base = -> Chamfer034005002025
  Edges = 1 edges: [Edge3 r1=1 r2=2]
FEATURE [Part::Chamfer] Chamfer034005002027
  Base = -> Chamfer034005002024
  Edges = 1 edges: [Edge15 r1=1 r2=2]
FEATURE [Part::MultiFuse] Fusion021005009009
  Shapes = -> [Chamfer034005002017,Chamfer034005002022,Chamfer034005002023,Chamfer034005002027,Chamfer034005002026]
FEATURE [Part::Cylinder] Cylinder035
  Angle = 360
  AttacherType = Attacher::AttachEngine3D
  Height = 10
  Placement = pos=(35,1e-15,5) rot=(-1,0,0;1.5708rad)
  Radius = 0.6
FEATURE [Part::Cylinder] Cylinder036
  Angle = 360
  AttacherType = Attacher::AttachEngine3D
  Height = 10
  Placement = pos=(35,-3e-15,15) rot=(-1,0,0;1.5708rad)
  Radius = 0.6
FEATURE [Part::Box] Box051028  label="Cube085"
  AttacherType = Attacher::AttachEngine3D
  Height = 10
  Length = 1.2
  Placement = pos=(34.4,0,5) rot=(0,0,1;0rad)
  Width = 1
FEATURE [Part::Box] Box051029  label="Cube086"
  AttacherType = Attacher::AttachEngine3D
  Height = 10
  Length = 1.2
  Placement = pos=(34.4,8,5) rot=(0,0,1;0rad)
  Width = 1
FEATURE [Part::MultiFuse] Fusion021005009010
  Shapes = -> [Cylinder035,Box051028,Cylinder036,Box051029]
FEATURE [Part::Cut] Cut018011002007
  Base = -> Fusion021005009009
  Tool = -> Fusion021005009010
FEATURE [Part::FeaturePython] Clone  label="vertical-clip"  # Draft clone (typed FeaturePython)
  AttacherType = Attacher::AttachEngine3D
  Fuse = false
  Objects = -> [Cut018011002007]
  Scale = (1,1,1)
FEATURE [Part::Box] Box051030  label="Cube087"
  AttacherType = Attacher::AttachEngine3D
  Height = 30
  Length = 40
  Placement = pos=(0,-0.5,14) rot=(0,0,1;0rad)
  Width = 3.5
FEATURE [Part::Cylinder] Cylinder037
  Angle = 360
  AttacherType = Attacher::AttachEngine3D
  Height = 29
  Placement = pos=(3.5,-0.5,14.5) rot=(0,0,1;0rad)
  Radius = 3.5
FEATURE [Part::Cylinder] Cylinder038
  Angle = 360
  AttacherType = Attacher::AttachEngine3D
  Height = 31
  Placement = pos=(3.5,-0.5,13.5) rot=(0,0,1;0rad)
  Radius = 1.65
FEATURE [Part::Box] Box051031  label="Cube088"
  AttacherType = Attacher::AttachEngine3D
  Height = 58
  Length = 16
  Placement = pos=(12,3,0) rot=(0,0,1;0rad)
  Width = 3
FEATURE [Part::Box] Box051032  label="Cube089"
  AttacherType = Attacher::AttachEngine3D
  Height = 8
  Length = 8
  Placement = pos=(16,6,0) rot=(0,0,1;0rad)
  Width = 2
FEATURE [Part::Box] Box051033  label="Cube090"
  AttacherType = Attacher::AttachEngine3D
  Height = 8
  Length = 8
  Placement = pos=(16,6,50) rot=(0,0,1;0rad)
  Width = 2
FEATURE [Part::Box] Box051034  label="Cube091"
  AttacherType = Attacher::AttachEngine3D
  Height = 14
  Length = 33
  Placement = pos=(7,-0.5,0) rot=(0,0,1;0rad)
  Width = 3.5
FEATURE [Part::Box] Box051035  label="Cube092"
  AttacherType = Attacher::AttachEngine3D
  Height = 14
  Length = 33
  Placement = pos=(7,-0.5,44) rot=(0,0,1;0rad)
  Width = 3.5
FEATURE [Part::Cylinder] Cylinder039
  Angle = 360
  AttacherType = Attacher::AttachEngine3D
  Height = 14
  Placement = pos=(3.5,-0.5,0) rot=(0,0,1;0rad)
  Radius = 3.5
FEATURE [Part::Cylinder] Cylinder040
  Angle = 360
  AttacherType = Attacher::AttachEngine3D
  Height = 14
  Placement = pos=(3.5,-0.5,44) rot=(0,0,1;0rad)
  Radius = 3.5
FEATURE [Part::Cylinder] Cylinder041
  Angle = 360
  AttacherType = Attacher::AttachEngine3D
  Height = 15
  Placement = pos=(3.5,-0.5,43.5) rot=(0,0,1;0rad)
  Radius = 1.65
FEATURE [Part::Cylinder] Cylinder042
  Angle = 360
  AttacherType = Attacher::AttachEngine3D
  Height = 15
  Placement = pos=(3.5,-0.5,0) rot=(0,0,1;0rad)
  Radius = 1.5
FEATURE [Part::Box] Box051036  label="Cube093"
  AttacherType = Attacher::AttachEngine3D
  Height = 58
  Length = 45
  Placement = pos=(5,-7.5,0) rot=(0,0,1;0rad)
  Width = 3.5
FEATURE [Part::Box] Box051037  label="Cube094"
  AttacherType = Attacher::AttachEngine3D
  Height = 14
  Length = 7
  Placement = pos=(0,-7.5,0) rot=(0,0,1;0rad)
  Width = 6.5
FEATURE [Part::Box] Box051038  label="Cube095"
  AttacherType = Attacher::AttachEngine3D
  Height = 14
  Length = 7
  Placement = pos=(0,-7.5,44) rot=(0,0,1;0rad)
  Width = 6.5
FEATURE [Part::Cylinder] Cylinder043
  Angle = 360
  AttacherType = Attacher::AttachEngine3D
  Height = 19
  Placement = pos=(20,-3,4) rot=(-1,0,0;1.5708rad)
  Radius = 1.7
FEATURE [Part::Cylinder] Cylinder044
  Angle = 360
  AttacherType = Attacher::AttachEngine3D
  Height = 19
  Placement = pos=(20,-3,54) rot=(-1,0,0;1.5708rad)
  Radius = 1.7
FEATURE [Part::Cylinder] Cylinder045
  Angle = 360
  AttacherType = Attacher::AttachEngine3D
  Height = 4
  Placement = pos=(20,-3,54) rot=(-1,0,0;1.5708rad)
  Radius = 3
FEATURE [Part::Cylinder] Cylinder046
  Angle = 360
  AttacherType = Attacher::AttachEngine3D
  Height = 4
  Placement = pos=(20,-3,4) rot=(-1,0,0;1.5708rad)
  Radius = 3
FEATURE [Part::Cylinder] Cylinder047
  Angle = 360
  AttacherType = Attacher::AttachEngine3D
  Height = 10
  Placement = pos=(45,2e-15,5) rot=(1,0,0;1.5708rad)
  Radius = 1.7
FEATURE [Part::Cylinder] Cylinder048
  Angle = 360
  AttacherType = Attacher::AttachEngine3D
  Height = 10
  Placement = pos=(45,1.22e-14,53) rot=(1,0,0;1.5708rad)
  Radius = 1.7
FEATURE [Part::Box] Box051039  label="Cube096"
  AttacherType = Attacher::AttachEngine3D
  Height = 10
  Length = 12
  Placement = pos=(14,-1,24) rot=(0,0,1;0rad)
  Width = 10
FEATURE [Part::Cylinder] Cylinder049
  Angle = 360
  AttacherType = Attacher::AttachEngine3D
  Height = 10
  Placement = pos=(20,6e-15,29) rot=(1,0,0;1.5708rad)
  Radius = 1.7
FEATURE [Part::MultiFuse] Fusion021005009019
  Placement = pos=(0,2.5,0) rot=(0,0,1;0rad)
  Shapes = -> [Cylinder045,Cylinder046]
FEATURE [Part::MultiFuse] Fusion021005009020
  Shapes = -> [Cylinder043,Cylinder044]
FEATURE [Part::Box] Box051040  label="Cube097"
  AttacherType = Attacher::AttachEngine3D
  Height = 10
  Length = 10
  Placement = pos=(-3,-2,4.5) rot=(0,0,1;0rad)
  Width = 10
FEATURE [Part::Box] Box051041  label="Cube098"
  AttacherType = Attacher::AttachEngine3D
  Height = 10
  Length = 10
  Placement = pos=(-3,-2,43.5) rot=(0,0,1;0rad)
  Width = 10
FEATURE [Part::Cut] Cut018011002015
  Base = -> Box051030
  Tool = -> Box051041
FEATURE [Part::Cut] Cut018011002016
  Base = -> Cut018011002015
  Tool = -> Box051040
FEATURE [Part::MultiFuse] Fusion021005009021
  Shapes = -> [Cut018011002016,Cylinder037]
FEATURE [Part::Cut] Cut018011002017
  Base = -> Fusion021005009021
  Tool = -> Cylinder038
FEATURE [Part::Chamfer] Chamfer034005002038
  Base = -> Box051035
  Edges = 1 edges r=2: [Edge1]
FEATURE [Part::Chamfer] Chamfer034005002039
  Base = -> Box051034
  Edges = 1 edges r=2: [Edge1]
FEATURE [Part::Chamfer] Chamfer034005002040
  Base = -> Cut018011002017
  Edges = 1 edges r=1: [Edge22]
FEATURE [Part::MultiFuse] Fusion021005009022
  Shapes = -> [Chamfer034005002039,Chamfer034005002038,Chamfer034005002040,Box051032,Box051033,Box051031]
FEATURE [Part::Cut] Cut018011002018
  Base = -> Fusion021005009022
  Tool = -> Box051039
FEATURE [Part::MultiFuse] Fusion021005009023
  Shapes = -> [Fusion021005009020,Fusion021005009019]
FEATURE [Part::Cut] Cut018011002019
  Base = -> Cut018011002018
  Tool = -> Fusion021005009023
FEATURE [Part::Chamfer] Chamfer034005002041
  Base = -> Cut018011002019
  Edges = 1 edges r=5: [Edge86]
FEATURE [Part::Chamfer] Chamfer034005002042
  Base = -> Chamfer034005002041
  Edges = 2 edges r=1: [Edge95,Edge109]
FEATURE [Part::Chamfer] Chamfer034005002043
  Base = -> Box051038
  Edges = 1 edges r=5: [Edge1]
FEATURE [Part::Chamfer] Chamfer034005002044
  Base = -> Box051037
  Edges = 1 edges r=5: [Edge1]
FEATURE [Part::Chamfer] Chamfer034005002045
  Base = -> Chamfer034005002043
  Edges = 1 edges r=1: [Edge2]
FEATURE [Part::Chamfer] Chamfer034005002046
  Base = -> Chamfer034005002044
  Edges = 1 edges r=1: [Edge2]
FEATURE [Part::MultiFuse] Fusion021005009024
  Shapes = -> [Cylinder040,Chamfer034005002045]
FEATURE [Part::MultiFuse] Fusion021005009025
  Shapes = -> [Chamfer034005002046,Cylinder039]
FEATURE [Part::Chamfer] Chamfer034005002047
  Base = -> Box051036
  Edges = 1 edges r=1: [Edge3]
FEATURE [Part::Cut] Cut018011002020
  Base = -> Fusion021005009024
  Tool = -> Cylinder041
FEATURE [Part::Cut] Cut018011002021
  Base = -> Fusion021005009025
  Tool = -> Cylinder042
FEATURE [Part::Box] Box051042  label="Cube099"
  AttacherType = Attacher::AttachEngine3D
  Height = 10
  Length = 10
  Placement = pos=(-1.5,-9.5,56) rot=(0,0,1;0rad)
  Width = 24
FEATURE [Part::Cut] Cut018011002022
  Base = -> Cut018011002020
  Tool = -> Box051042
FEATURE [Part::MultiFuse] Fusion021005009027
  Shapes = -> [Cylinder049,Cylinder047,Cylinder048]
FEATURE [Part::MultiFuse] Fusion021005009028
  Shapes = -> [Cut018011002022,Cut018011002021,Chamfer034005002047]
FEATURE [Part::Cut] Cut018011002023
  Base = -> Fusion021005009028
  Tool = -> Fusion021005009027
FEATURE [Part::Chamfer] Chamfer034005002048
  Base = -> Cut018011002023
  Edges = 2 edges r=1: [Edge59,Edge65]
FEATURE [Part::Chamfer] Chamfer034005002049
  Base = -> Chamfer034005002042
  Edges = 2 edges r=1: [Edge79,Edge83]
FEATURE [Part::Feature] Chamfer034005002048001  label="Chamfer034005002050"
  shape: bbox 50 x 10.5 x 58 mm, 45 faces (baked)
FEATURE [Part::Box] Box051067  label="Cube124"
  AttacherType = Attacher::AttachEngine3D
  Height = 58
  Length = 3
  Placement = pos=(4,-7.5,0) rot=(0,0,1;0rad)
  Width = 9
FEATURE [Part::Box] Box051068  label="Cube125"
  AttacherType = Attacher::AttachEngine3D
  Height = 58
  Length = 8
  Placement = pos=(-1,-7.5,0) rot=(0,0,1;0rad)
  Width = 15
FEATURE [Part::Cut] Cut018011002025
  Base = -> Chamfer034005002048001
  Tool = -> Box051068
FEATURE [Part::MultiFuse] Fusion021005009032
  Shapes = -> [Cut018011002025,Box051067]
FEATURE [Part::Chamfer] Chamfer034005002048002  label="door-drill-template"
  Base = -> Fusion021005009032
  Edges = 10 edges r=0.4: [Edge1,Edge2,Edge4,Edge5,Edge10,Edge18,Edge19,Edge20,Edge21,Edge22]
FEATURE [Part::Feature] Chamfer034005002048002001  label="door-drill-template001"
  shape: bbox 46 x 9 x 58 mm, 28 faces (baked)
FEATURE [Part::Box] Box051069  label="Cube126"
  AttacherType = Attacher::AttachEngine3D
  Height = 58
  Length = 9
  Placement = pos=(41,-5.5,0) rot=(0,0,1;0rad)
  Width = 1
FEATURE [Part::MultiCommon] Common002  label="door-back-support"
  Shapes = -> [Chamfer034005002048002001,Box051069]
FEATURE [Part::Box] Box051070  label="Cube127"
  AttacherType = Attacher::AttachEngine3D
  Height = 58
  Length = 10
  Placement = pos=(-3,-8,0) rot=(0,0,1;0rad)
  Width = 14
FEATURE [Part::Feature] Chamfer034005002048002002  label="Chamfer034005002051"
  shape: bbox 50 x 10.5 x 58 mm, 45 faces (baked)
FEATURE [Part::Feature] Chamfer034005002048002003  label="Chamfer034005002052"
  shape: bbox 50 x 10.5 x 58 mm, 45 faces (baked)
FEATURE [Part::Box] Box051071  label="Cube128"
  AttacherType = Attacher::AttachEngine3D
  Height = 58
  Length = 10
  Placement = pos=(-3,-8,0) rot=(0,0,1;0rad)
  Width = 14
FEATURE [Part::MultiCommon] Common003
  Placement = pos=(0,1,0) rot=(0,0,1;0rad)
  Shapes = -> [Box051070,Chamfer034005002048002002]
FEATURE [Part::Cut] Cut018011002026
  Base = -> Chamfer034005002048002003
  Tool = -> Box051071
FEATURE [Part::Box] Box051072  label="Cube129"
  AttacherType = Attacher::AttachEngine3D
  Height = 58
  Length = 2
  Placement = pos=(5,-7.5,0) rot=(0,0,1;0rad)
  Width = 1
FEATURE [Part::Chamfer] Chamfer034005002048002004
  Base = -> Box051072
  Edges = 1 edges r=0.4: [Edge1]
FEATURE [Part::MultiFuse] Fusion021005009033  label="door-mounter-extend"
  Shapes = -> [Common003,Chamfer034005002048002004,Cut018011002026]
